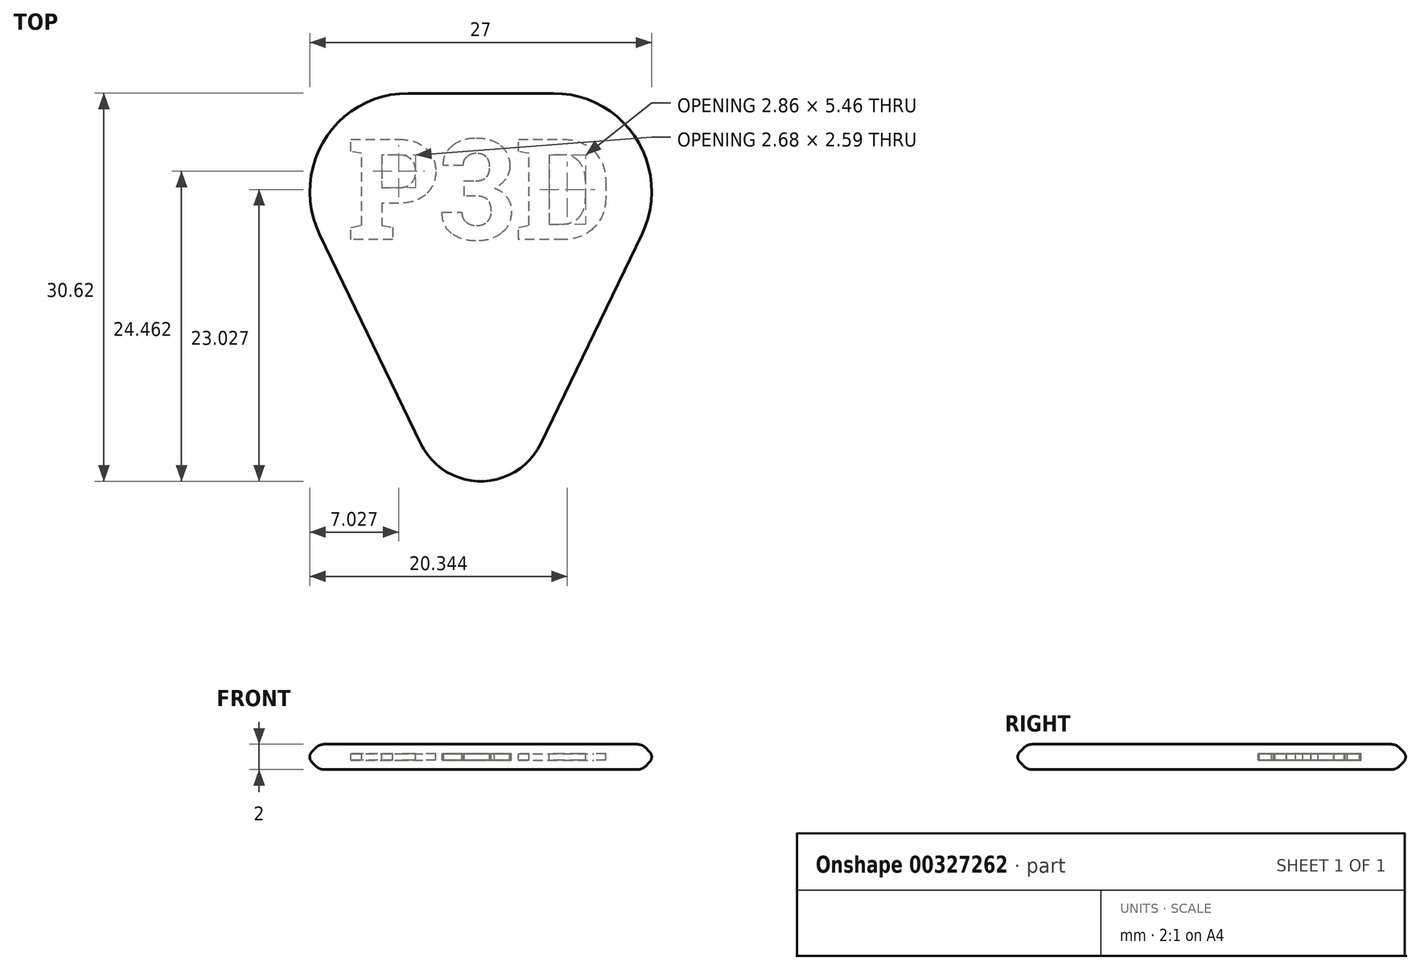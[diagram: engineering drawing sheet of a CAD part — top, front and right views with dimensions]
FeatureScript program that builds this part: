
annotation { "Feature Type Name" : "Feature", "Feature Type Description" : "" }
export const myFeature = defineFeature(function(context is Context, id is Id, definition is map)
    precondition{}
    {
        {
            var Q0;
            Q0=qCreatedBy(makeId("Top.planeOp"),FACE);
            var sketch = newSketch(context, id + "F0", { "sketchPlane" : qUnion([Q0])});
            skLineSegment(sketch, "E0", {"start": v(-5.74, 12.45) * mm, "end": v(5.74, 12.45) * mm});
            skLineSegment(sketch, "E1", {"start": v(12.95, 0.97) * mm, "end": v(4.95, -15.56) * mm});
            skLineSegment(sketch, "E2", {"start": v(-4.95, -15.56) * mm, "end": v(-12.95, 0.97) * mm});
            skPoint(sketch, "E3.visualSharp", {"position": v(-18.5, 12.45) * mm});
            skArc(sketch, "E3.filletArc", {"start": v(-5.74, 12.45) * mm, "mid": v(-12.52, 8.7) * mm, "end": v(-12.95, 0.97) * mm});
            skPoint(sketch, "E4.visualSharp", {"position": v(18.5, 12.45) * mm});
            skArc(sketch, "E4.filletArc", {"start": v(12.95, 0.97) * mm, "mid": v(12.52, 8.7) * mm, "end": v(5.74, 12.45) * mm});
            skPoint(sketch, "E5.visualSharp", {"position": v(0, -25.8) * mm});
            skArc(sketch, "E5.filletArc", {"start": v(-4.95, -15.56) * mm, "mid": v(0, -18.66) * mm, "end": v(4.95, -15.56) * mm});
            skSolve(sketch);
        }
        {
            var Q0;
            Q0=makeQuery(id+"F0.imprint","IMPRINT",FACE,{"disambiguationData":[TD([[makeQuery(id+"F0.imprint","IMPRINT",EDGE,{"derivedFrom":sQuery(id+"F0.wireOp",EDGE,"E0")}),-1.0]])]});
            extrude(context, id + "F1", {"entities" : qUnion([Q0]), "endBound" : BoundingType.SYMMETRIC, "depth" : 2 * mm});
        }
        {
            var Q0;
            Q0=makeQuery(id+"F1.opExtrude","CAP_EDGE",EDGE,{"disambiguationData":[OSD([sQuery(id+"F0.wireOp",EDGE,"E1")])],"isStart":false});
            var Q1;
            Q1=makeQuery(id+"F1.opExtrude","CAP_EDGE",EDGE,{"disambiguationData":[OSD([sQuery(id+"F0.wireOp",EDGE,"E1")])],"isStart":true});
            chamfer(context, id + "F2", {"entities" : qUnion([Q0, Q1]), "chamferType" : ChamferType.OFFSET_ANGLE, "width" : 1 * mm, "oppositeDirection" : false, "angle" : 45 * degree, "tangentPropagation" : true});
        }
        {
            var Q0;
            {var subQ0=sQuery(id+"F0.wireOp",EDGE,"E2");Q0=makeQuery(id+"F2.opChamfer","BLEND_EDGE",EDGE,{"blendedFrom":[makeQuery(id+"F1.opExtrude","CAP_EDGE",EDGE,{"disambiguationData":[OSD([subQ0])],"isStart":false}),makeQuery(id+"F1.opExtrude","CAP_FACE",FACE,{"disambiguationData":[OSD([sQuery(id+"F0.wireOp",EDGE,"E0"),sQuery(id+"F0.wireOp",EDGE,"E1"),subQ0,sQuery(id+"F0.wireOp",EDGE,"E3.filletArc"),sQuery(id+"F0.wireOp",EDGE,"E4.filletArc"),sQuery(id+"F0.wireOp",EDGE,"E5.filletArc")])],"isStart":false})],"blendedInto":[makeQuery(id+"F1.opExtrude","CAP_FACE",FACE,{"disambiguationData":[OSD([sQuery(id+"F0.wireOp",EDGE,"E0"),sQuery(id+"F0.wireOp",EDGE,"E1"),subQ0,sQuery(id+"F0.wireOp",EDGE,"E3.filletArc"),sQuery(id+"F0.wireOp",EDGE,"E4.filletArc"),sQuery(id+"F0.wireOp",EDGE,"E5.filletArc")])],"isStart":false})]});}
            var Q1;
            {var subQ0=sQuery(id+"F0.wireOp",EDGE,"E1");Q1=makeQuery(id+"F2.opChamfer","BLEND_EDGE",EDGE,{"blendedFrom":[makeQuery(id+"F1.opExtrude","CAP_EDGE",EDGE,{"disambiguationData":[OSD([subQ0])],"isStart":true}),makeQuery(id+"F1.opExtrude","CAP_FACE",FACE,{"disambiguationData":[OSD([sQuery(id+"F0.wireOp",EDGE,"E0"),subQ0,sQuery(id+"F0.wireOp",EDGE,"E2"),sQuery(id+"F0.wireOp",EDGE,"E3.filletArc"),sQuery(id+"F0.wireOp",EDGE,"E4.filletArc"),sQuery(id+"F0.wireOp",EDGE,"E5.filletArc")])],"isStart":true})],"blendedInto":[makeQuery(id+"F1.opExtrude","CAP_FACE",FACE,{"disambiguationData":[OSD([sQuery(id+"F0.wireOp",EDGE,"E0"),subQ0,sQuery(id+"F0.wireOp",EDGE,"E2"),sQuery(id+"F0.wireOp",EDGE,"E3.filletArc"),sQuery(id+"F0.wireOp",EDGE,"E4.filletArc"),sQuery(id+"F0.wireOp",EDGE,"E5.filletArc")])],"isStart":true})]});}
            fillet(context, id + "F3", {"entities" : qUnion([Q0, Q1]), "radius" : 1 * mm, "tangentPropagation" : true, "allowEdgeOverflow" : false});
        }
        {
            var Q0;
            Q0=qCreatedBy(makeId("Top.planeOp"),FACE);
            var sketch = newSketch(context, id + "F4", { "sketchPlane" : qUnion([Q0])});
            skText(sketch, "E6", { "text": "P3D", "fontName": "RobotoSlab-Bold.ttf"});
            const initialGuessF4  = {"E6": [-0.01054, 0.00067, 1, 0, 0.008]};
            skSetInitialGuess(sketch, initialGuessF4);
            skSolve(sketch);
        }
        {
            var Q0;
            Q0=qSketchRegion(id+"F4",true);
            extrude(context, id + "F5", {"entities" : qUnion([Q0]), "operationType" : NewBodyOperationType.REMOVE, "endBound" : BoundingType.SYMMETRIC, "oppositeDirection" : true, "depth" : 0.5 * mm});
        }
        {
            var Q0;
            {var subQ0=sQuery(id+"F0.wireOp",EDGE,"E2");Q0=makeQuery(id+"F2.opChamfer","BLEND_EDGE",EDGE,{"blendedFrom":[makeQuery(id+"F1.opExtrude","CAP_EDGE",EDGE,{"disambiguationData":[OSD([subQ0])],"isStart":true}),makeQuery(id+"F1.opExtrude","CAP_EDGE",EDGE,{"disambiguationData":[OSD([subQ0])],"isStart":false})],"blendedInto":[]});}
            fillet(context, id + "F6", {"entities" : qUnion([Q0]), "radius" : 0.6 * mm, "tangentPropagation" : true, "allowEdgeOverflow" : false});
        }
    });
